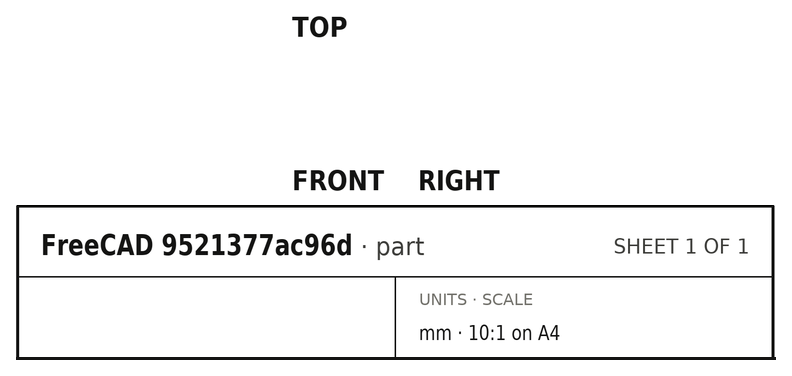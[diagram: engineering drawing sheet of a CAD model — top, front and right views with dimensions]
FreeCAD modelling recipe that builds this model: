
FCSTD DOCUMENT  (FreeCAD 0.21R33694 (Git))
Label: coaxial_waveguide
License: All rights reserved
LicenseURL: http://en.wikipedia.org/wiki/All_rights_reserved
objects: Part::Part2DObjectPython×5, App::FeaturePython×4, Part::Cut×1
note: 6 computed .brp shape members not serialized (recipe doc carries the construction recipe); baked Part::Feature solids carry a one-line shape summary decoded from their .brp

FEATURE [Part::Part2DObjectPython] Polygon  # Draft 2D object (typed FeaturePython)
  Area = 2.07615e-06
  ChamferSize = 0
  DrawMode = 0
  FacesNumber = 36
  FilletRadius = 0
  MakeFace = true
  Radius = 0.000815
FEATURE [Part::Part2DObjectPython] Polygon001  # Draft 2D object (typed FeaturePython)
  Area = 2.32953e-05
  ChamferSize = 0
  DrawMode = 0
  FacesNumber = 36
  FilletRadius = 0
  MakeFace = true
  Radius = 0.00273
FEATURE [Part::Part2DObjectPython] Polygon002  label="_Pinner"  # Draft 2D object (typed FeaturePython)
  Area = 0
  ChamferSize = 0
  DrawMode = 0
  FacesNumber = 36
  FilletRadius = 0
  MakeFace = false
  Radius = 0.000815
FEATURE [Part::Cut] Cut  label="coax"
  Base = -> Polygon001
  Tool = -> Polygon
FEATURE [Part::Part2DObjectPython] Line  label="_Pv"  # Draft 2D object (typed FeaturePython)
  Area = 0
  ChamferSize = 0
  Closed = false
  End = (0,-0.000815,0)
  FilletRadius = 0
  Length = 0.001915
  MakeFace = true
  Placement = pos=(0,-0.00273,0) rot=(0,0,1;0rad)
  Points = (2) [(0,0,0),(2.3452e-19,0.001915,0)]
  Start = (0,-0.00273,0)
  Subdivisions = 0
FEATURE [App::FeaturePython] Text  label="_M1(voltage){v}"  # WARN: FeaturePython — macro-defined, semantics opaque (R4)
  Placement = pos=(-0.0108812,-0.0266046,-0.025135) rot=(0.864922,0.231754,0.445197;1.08358rad)
  Text = .
FEATURE [App::FeaturePython] Text001  label="_M1(current){inner}"  # WARN: FeaturePython — macro-defined, semantics opaque (R4)
  Placement = pos=(-0.0108812,-0.0266046,-0.025135) rot=(0.864922,0.231754,0.445197;1.08358rad)
  Text = .
FEATURE [Part::Part2DObjectPython] Polygon003  label="_Pouter"  # Draft 2D object (typed FeaturePython)
  Area = 0
  ChamferSize = 0
  DrawMode = 0
  FacesNumber = 36
  FilletRadius = 0
  MakeFace = false
  Radius = 0.00273
FEATURE [App::FeaturePython] Text002  label="_Bi(SI,copper){inner}"  # WARN: FeaturePython — macro-defined, semantics opaque (R4)
  Placement = pos=(-0.0108812,-0.0266046,-0.025135) rot=(0.864922,0.231754,0.445197;1.08358rad)
  Text = .
FEATURE [App::FeaturePython] Text003  label="_Bo(SI,copper){outer}"  # WARN: FeaturePython — macro-defined, semantics opaque (R4)
  Placement = pos=(-0.0108812,-0.0266046,-0.025135) rot=(0.864922,0.231754,0.445197;1.08358rad)
  Text = .
